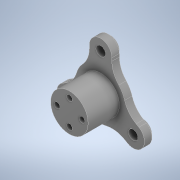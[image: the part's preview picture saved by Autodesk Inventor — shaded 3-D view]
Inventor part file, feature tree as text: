
AUTODESK INVENTOR PART (.ipt)
format: ipt  version: 2022 (Build 260153000, 153)  size: 179,712 bytes
history: mixed  units: in
note: dims shown in document units (in); Inventor stores cm internally (conversion verified against a paired STEP export)
features: extrude x4, sketch x4, chamfer x1, imported_body x1
ambient origin geometry x8: Origin, YZ Plane, XZ Plane, XY Plane, X Axis, Y Axis, Z Axis, Center Point
bodies: Solid1 (imported_parasolid)
feature tree (10):
  extrude  "Extrusion4"  Depth=0.3937in TaperAngle=0.0deg
  extrude  "Extrusion5"  Depth=0.4921in TaperAngle=0.0deg
  extrude  "Extrusion6"  Depth=1.5748in TaperAngle=360.0deg
  extrude  "Extrusion7"  [1 undecoded]
  sketch  "Sketch4"  dims[d8=0.0in d9=0.0in d10=0.3937in d11=0.0in]
  sketch  "Sketch5"  dims[d12=0.5906in d13=0.4921in d14=0.0in]
  sketch  "Sketch6"  dims[d16=0.0886in d17=1.5748in d19=360.0deg]
  sketch  "Sketch7"  dims[d21=0.0in d22=0.0in]
  chamfer  "Chamfer5"  [1 undecoded]
  imported_body  NMx_Import_Brep_tag  [imported B-rep: ~35 faces, bbox_mm=[31.788121, 26.496463, 16.5]]
note: 2 required parameter values undecoded (feature->parameter linkage not recoverable at this tier; creation-order binding heuristic only, values carry confidence <= 0.55)
